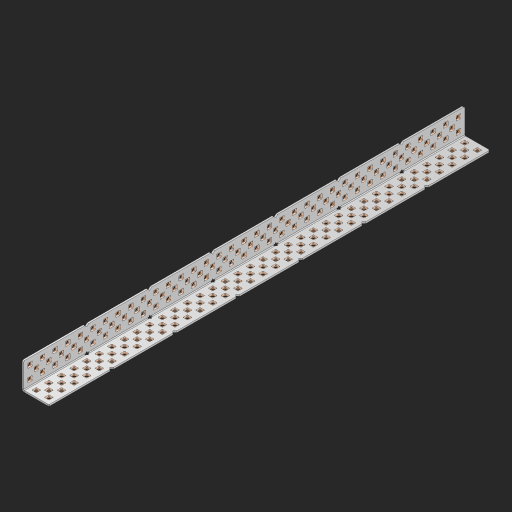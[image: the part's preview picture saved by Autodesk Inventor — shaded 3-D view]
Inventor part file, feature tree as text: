
AUTODESK INVENTOR PART (.ipt)
format: ipt  version: 2023 (Build 270158000, 158)  size: 2,310,144 bytes
history: native  units: in
note: dims shown in document units (in); Inventor stores cm internally (conversion verified against a paired STEP export)
features: other x214, extrude x206, sheet_metal_op x8, sketch x7, pattern_linear x2, mirror x1, chamfer x1
ambient origin geometry x8: Origin, YZ Plane, XZ Plane, XY Plane, X Axis, Y Axis, Z Axis, Center Point
bodies: Solid1 (feature_tree), Body (feature_tree)
feature tree (439):
  sheet_metal_op  "Flanges"
  sheet_metal_op  "Body Pattern"
  pattern_linear  "Center Pattern"  Spacing1=1.0in  [1 undecoded]
  other  "Arc Length"
  pattern_linear  "Notch Pattern"  Spacing1=0.25in  [1 undecoded]
  other  "Diagonal Plane"
  mirror  "Everything Mirrored"
  chamfer  "End Chamfer"
  sketch  "Sketch1"  dims[d0=1.0in]
  other  "Plate1"
  sketch  "Sketch2"  dims[d1=17.5in]
  other  "Plate2"
  sheet_metal_op  "Bend1"
  sheet_metal_op  "Corner1"
  sketch  "Sketch8"  dims[d2=0.0625in]
  sketch  "Sketch9"  dims[d3=0.0625in]
  other  "Srf91"
  sheet_metal_op  "Body Pattern Sketch"
  other  "Srf92"
  sketch  "Sketch13"  dims[d4=0.0312in]
  sketch  "Sketch15"  dims[d5=0.125in]
  sketch  "Sketch16"  dims[d6=0.0625in d7=1.0in d8=90.0deg d9=0.0312in d10=0.25in d11=0.0625in d12=0.0625in d49=0.182in d50=0.02in d52=0.25in d53=0.0625in d54=0.0in d55=0.172in d56=1.0in d57=0.0in d60=13.7795in d62=0.5in d63=0.7874in d65=0.5in d85=0.1473in d86=0.1782in d89=0.0625in d90=0.0in d91=0.04in d92=0.0491in d95=2.5in d96=0.04in d97=0.25in d98=45.0deg d99=0.25in d106=0.182in d107=0.02in d108=0.5in d110=0.0625in d111=0.0in d112=0.172in d113=0.5in d114=0.0in d117=0.5in d123=0.25in d125=0.25in d126=0.0491in d127=0.1473in d128=0.08in d129=0.04in d130=2.5in]
  other  "Srf786"
  other  "Srf856"
  other  "Srf857"
  other  "Srf858"
  other  "Srf859"
  other  "Srf860"
  other  "Srf861"
  other  "Srf889"
  other  "Srf890"
  other  "Srf891"
  other  "Srf1275"
  other  "Srf1276"
  other  "Srf1278"
  other  "Srf1279"
  other  "Srf1280"
  other  "Srf1281"
  other  "Srf1282"
  other  "Srf1283"
  other  "Srf1277"
  other  "Srf1285"
  other  "Srf1286"
  other  "Srf1287"
  other  "Srf1383"
  other  "Srf1384"
  other  "Srf1385"
  other  "Srf1386"
  other  "Srf1387"
  other  "Srf1388"
  other  "Srf1389"
  other  "Srf1390"
  other  "Srf1391"
  other  "Srf1392"
  other  "Srf1393"
  other  "Srf1394"
  other  "Srf1395"
  other  "Srf1396"
  other  "Srf1397"
  other  "Srf1398"
  other  "Srf1399"
  other  "Srf1400"
  other  "Srf1401"
  other  "Srf1402"
  other  "Srf1403"
  other  "Srf1404"
  other  "Srf1405"
  other  "Srf1406"
  other  "Srf1407"
  other  "Srf1408"
  other  "Srf1409"
  other  "Srf1410"
  other  "Srf1411"
  other  "Srf1412"
  other  "Srf1413"
  other  "Srf1414"
  other  "Srf1415"
  other  "Srf1416"
  other  "Srf1417"
  other  "Srf1418"
  other  "Srf1419"
  other  "Srf1420"
  other  "Srf1421"
  other  "Srf1422"
  other  "Srf1423"
  other  "Srf1424"
  other  "Srf1425"
  other  "Srf1426"
  other  "Srf1427"
  other  "Srf1428"
  other  "Srf1429"
  other  "Srf1430"
  other  "Srf1431"
  other  "Srf1432"
  other  "Srf1433"
  other  "Srf1434"
  other  "Srf1435"
  other  "Srf1436"
  other  "Srf1437"
  other  "Srf1438"
  other  "Srf1439"
  other  "Srf1440"
  other  "Srf1441"
  other  "Srf1442"
  other  "Srf1443"
  other  "Srf1444"
  other  "Srf1445"
  other  "Srf1446"
  other  "Srf1447"
  other  "Srf1448"
  other  "Srf1449"
  other  "Srf1450"
  other  "Srf1451"
  other  "Srf1452"
  other  "Srf1453"
  other  "Srf1454"
  other  "Srf1455"
  other  "Srf1456"
  other  "Srf1457"
  other  "Srf1458"
  other  "Srf1459"
  other  "Srf1460"
  other  "Srf1461"
  other  "Srf1462"
  other  "Srf1463"
  other  "Srf1464"
  other  "Srf1465"
  other  "Srf1466"
  other  "Srf1467"
  other  "Srf1468"
  other  "Srf1469"
  other  "Srf1470"
  other  "Srf1471"
  other  "Srf1472"
  other  "Srf1473"
  other  "Srf1474"
  other  "Srf1475"
  other  "Srf1476"
  other  "Srf1477"
  other  "Srf1478"
  other  "Srf1479"
  other  "Srf1480"
  other  "Srf1481"
  other  "Srf1482"
  other  "Srf1483"
  other  "Srf1484"
  other  "Srf1485"
  other  "Srf1486"
  other  "Srf1487"
  other  "Srf1488"
  other  "Srf1489"
  other  "Srf1490"
  other  "Srf1491"
  other  "Srf1492"
  other  "Srf1493"
  other  "Srf1494"
  other  "Srf1495"
  other  "Srf1496"
  other  "Srf1497"
  other  "Srf1498"
  other  "Srf1499"
  other  "Srf1500"
  other  "Srf1501"
  other  "Srf1502"
  other  "Srf1503"
  other  "Srf1504"
  other  "Srf1505"
  other  "Srf1506"
  other  "Srf1507"
  other  "Srf1508"
  other  "Srf1509"
  other  "Srf1510"
  other  "Srf1511"
  other  "Srf1512"
  other  "Srf1513"
  other  "Srf1514"
  other  "Srf1515"
  other  "Srf1516"
  other  "Srf1517"
  other  "Srf1518"
  other  "Srf1519"
  other  "Srf1520"
  other  "Srf1521"
  other  "Srf1522"
  other  "Srf1523"
  other  "Srf1524"
  other  "Srf1525"
  other  "Srf1526"
  other  "Srf1527"
  other  "Srf1528"
  other  "Srf1529"
  other  "Srf1530"
  other  "Srf1531"
  other  "Srf1532"
  other  "Srf1533"
  other  "Srf1534"
  other  "Srf1535"
  other  "Srf1536"
  other  "Srf1537"
  other  "Srf1538"
  other  "Srf1539"
  other  "Srf1540"
  other  "Srf1541"
  other  "Srf1542"
  other  "Srf1543"
  other  "Srf1544"
  other  "Srf1545"
  other  "Srf1546"
  other  "Srf1547"
  other  "Srf1548"
  other  "Srf1549"
  other  "Srf1550"
  other  "Srf1551"
  other  "Srf1552"
  other  "Srf1553"
  other  "Srf1554"
  other  "Srf1555"
  other  "Srf1556"
  other  "Srf1557"
  other  "Srf1558"
  other  "Srf1559"
  other  "Srf1560"
  other  "Srf1561"
  other  "Srf1562"
  other  "Srf1563"
  other  "Srf1564"
  other  "Srf1565"
  other  "Srf1566"
  sheet_metal_op  "Body Stamp"
  sheet_metal_op  "Body Circle"
  other  "Center Stamp"
  other  "Center Circle"
  sheet_metal_op  "Notch"
  extrude  "ExtrusionSrf92"  Depth=0.0625in
  extrude  "ExtrusionSrf856"  Depth=0.0625in
  extrude  "ExtrusionSrf857"  Depth=2.5in
  extrude  "ExtrusionSrf858"  Depth=0.02in
  extrude  "ExtrusionSrf859"  Depth=2.5in
  extrude  "ExtrusionSrf860"  Depth=0.0625in
  extrude  "ExtrusionSrf861"  TaperAngle=0.0deg  [1 undecoded]
  extrude  "ExtrusionSrf889"  Depth=2.5in
  extrude  "ExtrusionSrf890"  Depth=1.0in TaperAngle=0.0deg
  extrude  "ExtrusionSrf891"  Depth=2.5in
  extrude  "ExtrusionSrf1275"  Depth=0.5in
  extrude  "ExtrusionSrf1276"  Depth=2.5in
  extrude  "ExtrusionSrf1277"  Depth=2.5in
  extrude  "ExtrusionSrf1278"  Depth=0.0625in
  extrude  "ExtrusionSrf1279"  Depth=2.5in TaperAngle=0.0deg
  extrude  "ExtrusionSrf1280"  Depth=2.5in
  extrude  "ExtrusionSrf1281"  Depth=2.5in TaperAngle=45.0deg
  extrude  "ExtrusionSrf1282"  Depth=2.5in
  extrude  "ExtrusionSrf1345"  Depth=2.5in
  extrude  "ExtrusionSrf1346"  Depth=0.02in
  extrude  "ExtrusionSrf1347"  Depth=0.5in
  extrude  "ExtrusionSrf1348"  Depth=0.0625in
  extrude  "ExtrusionSrf1383"  TaperAngle=0.0deg  [1 undecoded]
  extrude  "ExtrusionSrf1384"  Depth=2.5in
  extrude  "ExtrusionSrf1385"  Depth=0.5in TaperAngle=0.0deg
  extrude  "ExtrusionSrf1386"  Depth=0.5in
  extrude  "ExtrusionSrf1387"  Depth=2.5in
  extrude  "ExtrusionSrf1388"  Depth=2.5in
  extrude  "ExtrusionSrf1389"  Depth=2.5in
  extrude  "ExtrusionSrf1390"  Depth=2.5in
  extrude  "ExtrusionSrf1391"  Depth=2.5in
  extrude  "ExtrusionSrf1392"  Depth=2.5in
  extrude  "ExtrusionSrf1393"  Depth=2.5in
  extrude  "ExtrusionSrf1394"  [1 undecoded]
  extrude  "ExtrusionSrf1395"  [1 undecoded]
  extrude  "ExtrusionSrf1396"  [1 undecoded]
  extrude  "ExtrusionSrf1397"  [1 undecoded]
  extrude  "ExtrusionSrf1398"  [1 undecoded]
  extrude  "ExtrusionSrf1399"  [1 undecoded]
  extrude  "ExtrusionSrf1400"  [1 undecoded]
  extrude  "ExtrusionSrf1401"  [1 undecoded]
  extrude  "ExtrusionSrf1402"  [1 undecoded]
  extrude  "ExtrusionSrf1403"  [1 undecoded]
  extrude  "ExtrusionSrf1404"  [1 undecoded]
  extrude  "ExtrusionSrf1405"  [1 undecoded]
  extrude  "ExtrusionSrf1406"  [1 undecoded]
  extrude  "ExtrusionSrf1407"  [1 undecoded]
  extrude  "ExtrusionSrf1408"  [1 undecoded]
  extrude  "ExtrusionSrf1409"  [1 undecoded]
  extrude  "ExtrusionSrf1410"  [1 undecoded]
  extrude  "ExtrusionSrf1411"  [1 undecoded]
  extrude  "ExtrusionSrf1412"  [1 undecoded]
  extrude  "ExtrusionSrf1413"  [1 undecoded]
  extrude  "ExtrusionSrf1414"  [1 undecoded]
  extrude  "ExtrusionSrf1415"  [1 undecoded]
  extrude  "ExtrusionSrf1416"  [1 undecoded]
  extrude  "ExtrusionSrf1417"  [1 undecoded]
  extrude  "ExtrusionSrf1418"  [1 undecoded]
  extrude  "ExtrusionSrf1419"  [1 undecoded]
  extrude  "ExtrusionSrf1420"  [1 undecoded]
  extrude  "ExtrusionSrf1421"  [1 undecoded]
  extrude  "ExtrusionSrf1422"  [1 undecoded]
  extrude  "ExtrusionSrf1423"  [1 undecoded]
  extrude  "ExtrusionSrf1424"  [1 undecoded]
  extrude  "ExtrusionSrf1425"  [1 undecoded]
  extrude  "ExtrusionSrf1426"  [1 undecoded]
  extrude  "ExtrusionSrf1427"  [1 undecoded]
  extrude  "ExtrusionSrf1428"  [1 undecoded]
  extrude  "ExtrusionSrf1429"  [1 undecoded]
  extrude  "ExtrusionSrf1430"  [1 undecoded]
  extrude  "ExtrusionSrf1431"  [1 undecoded]
  extrude  "ExtrusionSrf1432"  [1 undecoded]
  extrude  "ExtrusionSrf1433"  [1 undecoded]
  extrude  "ExtrusionSrf1434"  [1 undecoded]
  extrude  "ExtrusionSrf1435"  [1 undecoded]
  extrude  "ExtrusionSrf1436"  [1 undecoded]
  extrude  "ExtrusionSrf1437"  [1 undecoded]
  extrude  "ExtrusionSrf1438"  [1 undecoded]
  extrude  "ExtrusionSrf1439"  [1 undecoded]
  extrude  "ExtrusionSrf1440"  [1 undecoded]
  extrude  "ExtrusionSrf1441"  [1 undecoded]
  extrude  "ExtrusionSrf1442"  [1 undecoded]
  extrude  "ExtrusionSrf1443"  [1 undecoded]
  extrude  "ExtrusionSrf1444"  [1 undecoded]
  extrude  "ExtrusionSrf1445"  [1 undecoded]
  extrude  "ExtrusionSrf1446"  [1 undecoded]
  extrude  "ExtrusionSrf1447"  [1 undecoded]
  extrude  "ExtrusionSrf1448"  [1 undecoded]
  extrude  "ExtrusionSrf1449"  [1 undecoded]
  extrude  "ExtrusionSrf1450"  [1 undecoded]
  extrude  "ExtrusionSrf1451"  [1 undecoded]
  extrude  "ExtrusionSrf1452"  [1 undecoded]
  extrude  "ExtrusionSrf1453"  [1 undecoded]
  extrude  "ExtrusionSrf1454"  [1 undecoded]
  extrude  "ExtrusionSrf1455"  [1 undecoded]
  extrude  "ExtrusionSrf1456"  [1 undecoded]
  extrude  "ExtrusionSrf1457"  [1 undecoded]
  extrude  "ExtrusionSrf1458"  [1 undecoded]
  extrude  "ExtrusionSrf1459"  [1 undecoded]
  extrude  "ExtrusionSrf1460"  [1 undecoded]
  extrude  "ExtrusionSrf1461"  [1 undecoded]
  extrude  "ExtrusionSrf1462"  [1 undecoded]
  extrude  "ExtrusionSrf1463"  [1 undecoded]
  extrude  "ExtrusionSrf1464"  [1 undecoded]
  extrude  "ExtrusionSrf1465"  [1 undecoded]
  extrude  "ExtrusionSrf1466"  [1 undecoded]
  extrude  "ExtrusionSrf1467"  [1 undecoded]
  extrude  "ExtrusionSrf1468"  [1 undecoded]
  extrude  "ExtrusionSrf1469"  [1 undecoded]
  extrude  "ExtrusionSrf1470"  [1 undecoded]
  extrude  "ExtrusionSrf1471"  [1 undecoded]
  extrude  "ExtrusionSrf1472"  [1 undecoded]
  extrude  "ExtrusionSrf1473"  [1 undecoded]
  extrude  "ExtrusionSrf1474"  [1 undecoded]
  extrude  "ExtrusionSrf1475"  [1 undecoded]
  extrude  "ExtrusionSrf1476"  [1 undecoded]
  extrude  "ExtrusionSrf1477"  [1 undecoded]
  extrude  "ExtrusionSrf1478"  [1 undecoded]
  extrude  "ExtrusionSrf1479"  [1 undecoded]
  extrude  "ExtrusionSrf1480"  [1 undecoded]
  extrude  "ExtrusionSrf1481"  [1 undecoded]
  extrude  "ExtrusionSrf1482"  [1 undecoded]
  extrude  "ExtrusionSrf1483"  [1 undecoded]
  extrude  "ExtrusionSrf1484"  [1 undecoded]
  extrude  "ExtrusionSrf1485"  [1 undecoded]
  extrude  "ExtrusionSrf1486"  [1 undecoded]
  extrude  "ExtrusionSrf1487"  [1 undecoded]
  extrude  "ExtrusionSrf1488"  [1 undecoded]
  extrude  "ExtrusionSrf1489"  [1 undecoded]
  extrude  "ExtrusionSrf1490"  [1 undecoded]
  extrude  "ExtrusionSrf1491"  [1 undecoded]
  extrude  "ExtrusionSrf1492"  [1 undecoded]
  extrude  "ExtrusionSrf1493"  [1 undecoded]
  extrude  "ExtrusionSrf1494"  [1 undecoded]
  extrude  "ExtrusionSrf1495"  [1 undecoded]
  extrude  "ExtrusionSrf1496"  [1 undecoded]
  extrude  "ExtrusionSrf1497"  [1 undecoded]
  extrude  "ExtrusionSrf1498"  [1 undecoded]
  extrude  "ExtrusionSrf1499"  [1 undecoded]
  extrude  "ExtrusionSrf1500"  [1 undecoded]
  extrude  "ExtrusionSrf1501"  [1 undecoded]
  extrude  "ExtrusionSrf1502"  [1 undecoded]
  extrude  "ExtrusionSrf1503"  [1 undecoded]
  extrude  "ExtrusionSrf1504"  [1 undecoded]
  extrude  "ExtrusionSrf1505"  [1 undecoded]
  extrude  "ExtrusionSrf1506"  [1 undecoded]
  extrude  "ExtrusionSrf1507"  [1 undecoded]
  extrude  "ExtrusionSrf1508"  [1 undecoded]
  extrude  "ExtrusionSrf1509"  [1 undecoded]
  extrude  "ExtrusionSrf1510"  [1 undecoded]
  extrude  "ExtrusionSrf1511"  [1 undecoded]
  extrude  "ExtrusionSrf1512"  [1 undecoded]
  extrude  "ExtrusionSrf1513"  [1 undecoded]
  extrude  "ExtrusionSrf1514"  [1 undecoded]
  extrude  "ExtrusionSrf1515"  [1 undecoded]
  extrude  "ExtrusionSrf1516"  [1 undecoded]
  extrude  "ExtrusionSrf1517"  [1 undecoded]
  extrude  "ExtrusionSrf1518"  [1 undecoded]
  extrude  "ExtrusionSrf1519"  [1 undecoded]
  extrude  "ExtrusionSrf1520"  [1 undecoded]
  extrude  "ExtrusionSrf1521"  [1 undecoded]
  extrude  "ExtrusionSrf1522"  [1 undecoded]
  extrude  "ExtrusionSrf1523"  [1 undecoded]
  extrude  "ExtrusionSrf1524"  [1 undecoded]
  extrude  "ExtrusionSrf1525"  [1 undecoded]
  extrude  "ExtrusionSrf1526"  [1 undecoded]
  extrude  "ExtrusionSrf1527"  [1 undecoded]
  extrude  "ExtrusionSrf1528"  [1 undecoded]
  extrude  "ExtrusionSrf1529"  [1 undecoded]
  extrude  "ExtrusionSrf1530"  [1 undecoded]
  extrude  "ExtrusionSrf1531"  [1 undecoded]
  extrude  "ExtrusionSrf1532"  [1 undecoded]
  extrude  "ExtrusionSrf1533"  [1 undecoded]
  extrude  "ExtrusionSrf1534"  [1 undecoded]
  extrude  "ExtrusionSrf1535"  [1 undecoded]
  extrude  "ExtrusionSrf1536"  [1 undecoded]
  extrude  "ExtrusionSrf1537"  [1 undecoded]
  extrude  "ExtrusionSrf1538"  [1 undecoded]
  extrude  "ExtrusionSrf1539"  [1 undecoded]
  extrude  "ExtrusionSrf1540"  [1 undecoded]
  extrude  "ExtrusionSrf1541"  [1 undecoded]
  extrude  "ExtrusionSrf1542"  [1 undecoded]
  extrude  "ExtrusionSrf1543"  [1 undecoded]
  extrude  "ExtrusionSrf1544"  [1 undecoded]
  extrude  "ExtrusionSrf1545"  [1 undecoded]
  extrude  "ExtrusionSrf1546"  [1 undecoded]
  extrude  "ExtrusionSrf1547"  [1 undecoded]
  extrude  "ExtrusionSrf1548"  [1 undecoded]
  extrude  "ExtrusionSrf1549"  [1 undecoded]
  extrude  "ExtrusionSrf1550"  [1 undecoded]
  extrude  "ExtrusionSrf1551"  [1 undecoded]
  extrude  "ExtrusionSrf1552"  [1 undecoded]
  extrude  "ExtrusionSrf1553"  [1 undecoded]
  extrude  "ExtrusionSrf1554"  [1 undecoded]
  extrude  "ExtrusionSrf1555"  [1 undecoded]
  extrude  "ExtrusionSrf1556"  [1 undecoded]
  extrude  "ExtrusionSrf1557"  [1 undecoded]
  extrude  "ExtrusionSrf1558"  [1 undecoded]
  extrude  "ExtrusionSrf1559"  [1 undecoded]
  extrude  "ExtrusionSrf1560"  [1 undecoded]
  extrude  "ExtrusionSrf1561"  [1 undecoded]
  extrude  "ExtrusionSrf1562"  [1 undecoded]
  extrude  "ExtrusionSrf1563"  [1 undecoded]
  extrude  "ExtrusionSrf1564"  [1 undecoded]
  extrude  "ExtrusionSrf1565"  [1 undecoded]
  extrude  "ExtrusionSrf1566"  [1 undecoded]
note: 177 required parameter values undecoded (feature->parameter linkage not recoverable at this tier; creation-order binding heuristic only, values carry confidence <= 0.55)
